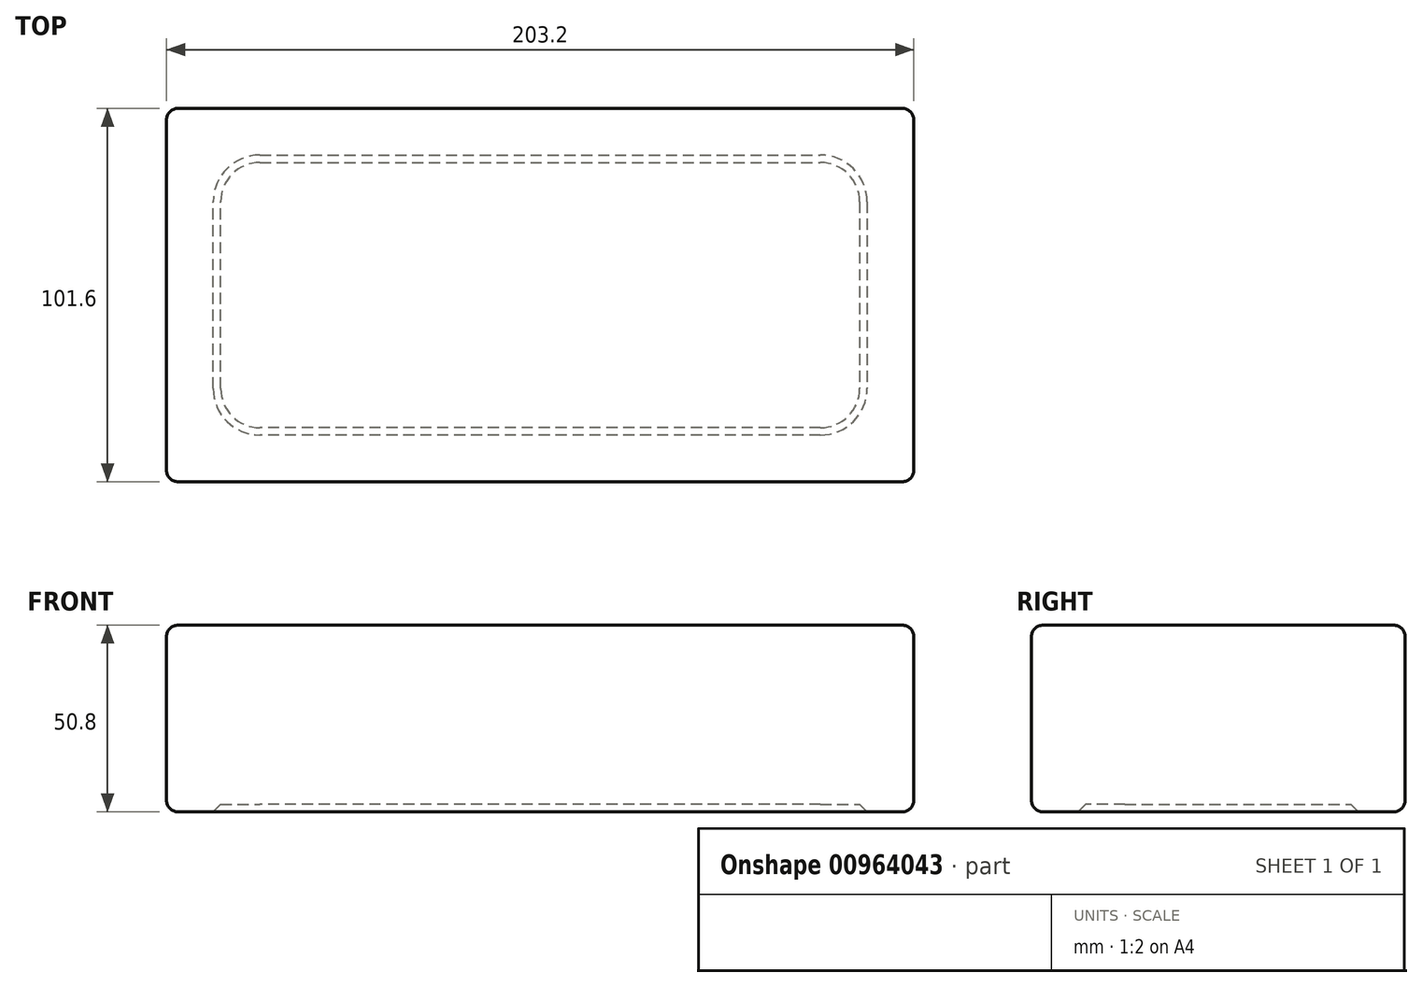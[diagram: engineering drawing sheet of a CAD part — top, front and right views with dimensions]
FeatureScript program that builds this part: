
annotation { "Feature Type Name" : "Feature", "Feature Type Description" : "" }
export const myFeature = defineFeature(function(context is Context, id is Id, definition is map)
    precondition{}
    {
        {
            var Q0;
            Q0=qCreatedBy(makeId("Top.planeOp"),FACE);
            var sketch = newSketch(context, id + "F0", { "sketchPlane" : qUnion([Q0])});
            skLineSegment(sketch, "E0.bottom", {"start": v(3.18, 0) * mm, "end": v(200.03, 0) * mm});
            skLineSegment(sketch, "E0.top", {"start": v(3.17, 101.6) * mm, "end": v(200.03, 101.6) * mm});
            skLineSegment(sketch, "E0.left", {"start": v(0, 3.17) * mm, "end": v(0, 98.43) * mm});
            skLineSegment(sketch, "E0.right", {"start": v(203.2, 3.18) * mm, "end": v(203.2, 98.43) * mm});
            skPoint(sketch, "E1.visualSharp", {"position": v(0, 101.6) * mm});
            skArc(sketch, "E1.filletArc", {"start": v(3.17, 101.6) * mm, "mid": v(0.93, 100.67) * mm, "end": v(0, 98.43) * mm});
            skPoint(sketch, "E2.visualSharp", {"position": v(0, 0) * mm});
            skArc(sketch, "E2.filletArc", {"start": v(0, 3.17) * mm, "mid": v(0.93, 0.93) * mm, "end": v(3.18, 0) * mm});
            skPoint(sketch, "E3.visualSharp", {"position": v(203.2, 0) * mm});
            skArc(sketch, "E3.filletArc", {"start": v(200.03, 0) * mm, "mid": v(202.27, 0.93) * mm, "end": v(203.2, 3.18) * mm});
            skPoint(sketch, "E4.visualSharp", {"position": v(203.2, 101.6) * mm});
            skArc(sketch, "E4.filletArc", {"start": v(203.2, 98.43) * mm, "mid": v(202.27, 100.67) * mm, "end": v(200.03, 101.6) * mm});
            skLineSegment(sketch, "E5.0", {"start": v(25.4, 88.9) * mm, "end": v(177.8, 88.9) * mm});
            skLineSegment(sketch, "E5.1", {"start": v(12.7, 25.4) * mm, "end": v(12.7, 76.2) * mm});
            skLineSegment(sketch, "E5.2", {"start": v(25.4, 12.7) * mm, "end": v(177.8, 12.7) * mm});
            skLineSegment(sketch, "E5.3", {"start": v(190.5, 25.4) * mm, "end": v(190.5, 76.2) * mm});
            skPoint(sketch, "E6.visualSharp", {"position": v(12.7, 88.9) * mm});
            skArc(sketch, "E6.filletArc", {"start": v(25.4, 88.9) * mm, "mid": v(16.42, 85.18) * mm, "end": v(12.7, 76.2) * mm});
            skPoint(sketch, "E7.visualSharp", {"position": v(12.7, 12.7) * mm});
            skArc(sketch, "E7.filletArc", {"start": v(12.7, 25.4) * mm, "mid": v(16.42, 16.42) * mm, "end": v(25.4, 12.7) * mm});
            skPoint(sketch, "E8.visualSharp", {"position": v(190.5, 12.7) * mm});
            skArc(sketch, "E8.filletArc", {"start": v(177.8, 12.7) * mm, "mid": v(186.78, 16.42) * mm, "end": v(190.5, 25.4) * mm});
            skPoint(sketch, "E9.visualSharp", {"position": v(190.5, 88.9) * mm});
            skArc(sketch, "E9.filletArc", {"start": v(190.5, 76.2) * mm, "mid": v(186.78, 85.18) * mm, "end": v(177.8, 88.9) * mm});
            skSolve(sketch);
        }
        {
            var Q0;
            Q0=makeQuery(id+"F0.imprint","IMPRINT",FACE,{"disambiguationData":[TD([[makeQuery(id+"F0.imprint","IMPRINT",EDGE,{"derivedFrom":sQuery(id+"F0.wireOp",EDGE,"E0.bottom")}),1.0]])]});
            var Q1;
            Q1=makeQuery(id+"F0.imprint","IMPRINT",FACE,{"disambiguationData":[TD([[makeQuery(id+"F0.imprint","IMPRINT",EDGE,{"derivedFrom":sQuery(id+"F0.wireOp",EDGE,"E5.0")}),-1.0]])]});
            extrude(context, id + "F1", {"entities" : qUnion([Q0, Q1]), "depth" : 50.8 * mm, "offsetDistance" : 25.4 * mm});
        }
        {
            var Q0;
            Q0=makeQuery(id+"F1.opExtrude","CAP_FACE",FACE,{"disambiguationData":[OSD([sQuery(id+"F0.wireOp",EDGE,"E0.bottom"),sQuery(id+"F0.wireOp",EDGE,"E0.top"),sQuery(id+"F0.wireOp",EDGE,"E0.left"),sQuery(id+"F0.wireOp",EDGE,"E0.right"),sQuery(id+"F0.wireOp",EDGE,"E1.filletArc"),sQuery(id+"F0.wireOp",EDGE,"E2.filletArc"),sQuery(id+"F0.wireOp",EDGE,"E3.filletArc"),sQuery(id+"F0.wireOp",EDGE,"E4.filletArc")])],"isStart":true});
            fillet(context, id + "F2", {"entities" : qUnion([Q0]), "tangentPropagation" : true, "radius" : 3.17 * mm, "defaultsChanged" : true, "vertexSettings" : [], "allowEdgeOverflow" : false});
        }
        {
            var Q0;
            Q0=makeQuery(id+"F1.opExtrude","CAP_FACE",FACE,{"disambiguationData":[OSD([sQuery(id+"F0.wireOp",EDGE,"E0.bottom"),sQuery(id+"F0.wireOp",EDGE,"E0.top"),sQuery(id+"F0.wireOp",EDGE,"E0.left"),sQuery(id+"F0.wireOp",EDGE,"E0.right"),sQuery(id+"F0.wireOp",EDGE,"E1.filletArc"),sQuery(id+"F0.wireOp",EDGE,"E2.filletArc"),sQuery(id+"F0.wireOp",EDGE,"E3.filletArc"),sQuery(id+"F0.wireOp",EDGE,"E4.filletArc")])],"isStart":false});
            fillet(context, id + "F3", {"entities" : qUnion([Q0]), "tangentPropagation" : true, "radius" : 3.17 * mm, "defaultsChanged" : true, "vertexSettings" : [], "allowEdgeOverflow" : false});
        }
        {
            var Q0;
            Q0=makeQuery(id+"F0.imprint","IMPRINT",FACE,{"disambiguationData":[TD([[makeQuery(id+"F0.imprint","IMPRINT",EDGE,{"derivedFrom":sQuery(id+"F0.wireOp",EDGE,"E5.0")}),-1.0]])]});
            extrude(context, id + "F4", {"entities" : qUnion([Q0]), "operationType" : NewBodyOperationType.REMOVE, "depth" : 2.03 * mm, "offsetDistance" : 25.4 * mm, "hasDraft" : true, "draftAngle" : 45 * degree, "draftPullDirection" : true});
        }
    });
